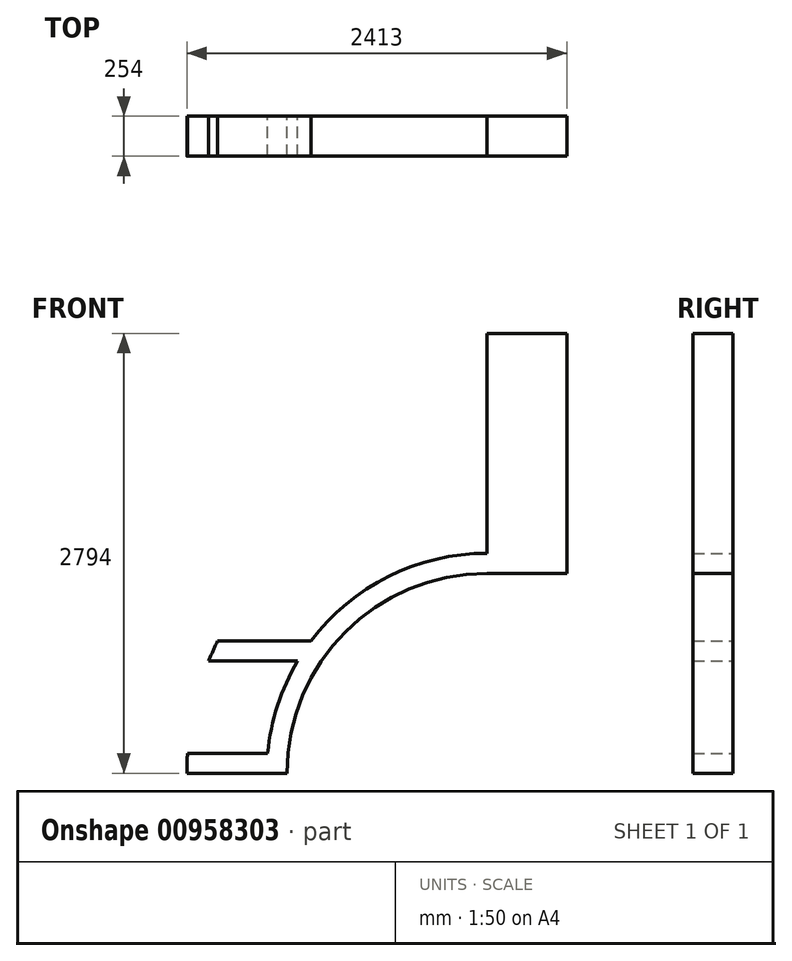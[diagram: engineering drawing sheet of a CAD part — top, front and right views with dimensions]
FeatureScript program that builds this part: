
annotation { "Feature Type Name" : "Feature", "Feature Type Description" : "" }
export const myFeature = defineFeature(function(context is Context, id is Id, definition is map)
    precondition{}
    {
        {
            var Q0;
            Q0=qCreatedBy(makeId("Front.planeOp"),FACE);
            var sketch = newSketch(context, id + "F0", { "sketchPlane" : qUnion([Q0])});
            skLineSegment(sketch, "E0", {"start": v(0, 0) * mm, "end": v(-2540, 0) * mm, "construction": true});
            skLineSegment(sketch, "E1", {"start": v(0, 0) * mm, "end": v(0, -2794) * mm, "construction": true});
            skLineSegment(sketch, "E2", {"start": v(-101.6, 0) * mm, "end": v(-101.6, -2655.82) * mm, "construction": true});
            skLineSegment(sketch, "E3", {"start": v(-304.8, 0) * mm, "end": v(-304.8, -2693.14) * mm, "construction": true});
            skLineSegment(sketch, "E4", {"start": v(-1748.8, 0) * mm, "end": v(-1748.79, -2667) * mm, "construction": true});
            skLineSegment(sketch, "E5", {"start": v(-762, 0) * mm, "end": v(-762, -2506.54) * mm, "construction": true});
            skLineSegment(sketch, "E6", {"start": v(-874.78, 0) * mm, "end": v(-874.78, -2403.9) * mm, "construction": true});
            skLineSegment(sketch, "E7", {"start": v(-508, 0) * mm, "end": v(-508, -2794) * mm});
            skLineSegment(sketch, "E8", {"start": v(-2540, 0) * mm, "end": v(-2540, -2684.02) * mm});
            skArc(sketch, "E9", {"start": v(-508, -1524) * mm, "mid": v(-1406.03, -1895.97) * mm, "end": v(-1778, -2794) * mm});
            skArc(sketch, "E10", {"start": v(-2540, -2794) * mm, "mid": v(-1944.84, -1357.16) * mm, "end": v(-508, -762) * mm});
            skArc(sketch, "E11", {"start": v(-2413, -2794) * mm, "mid": v(-1855.04, -1446.96) * mm, "end": v(-508, -889) * mm});
            skArc(sketch, "E12", {"start": v(-1905, -2794) * mm, "mid": v(-1495.83, -1806.17) * mm, "end": v(-508, -1397) * mm});
            skLineSegment(sketch, "E13", {"start": v(-2413, -2794) * mm, "end": v(-1905, -2794) * mm});
            skLineSegment(sketch, "E14", {"start": v(-1899.22, -2667) * mm, "end": v(-2408.76, -2667) * mm});
            skPoint(sketch, "E15.endSnap0", {"position": v(-1944.84, -1357.16) * mm});
            skLineSegment(sketch, "E16", {"start": v(-3837.1, -1954.53) * mm, "end": v(-1294.15, -1954.53) * mm, "construction": true});
            skLineSegment(sketch, "E17", {"start": v(-2218.06, -1954.53) * mm, "end": v(-1624.65, -1954.53) * mm});
            skLineSegment(sketch, "E18", {"start": v(-2274.75, -2081.53) * mm, "end": v(-1709.66, -2081.53) * mm});
            skLineSegment(sketch, "E19", {"start": v(-1624.65, -1954.53) * mm, "end": v(-1299.5, -1061.22) * mm});
            skLineSegment(sketch, "E20", {"start": v(-1466.04, -1147.43) * mm, "end": v(-1759.8, -1954.53) * mm});
            skLineSegment(sketch, "E21.bottom", {"start": v(-508, -1524) * mm, "end": v(0, -1524) * mm});
            skLineSegment(sketch, "E21.top", {"start": v(-508, 0) * mm, "end": v(0, 0) * mm});
            skLineSegment(sketch, "E21.left", {"start": v(-508, -1524) * mm, "end": v(-508, 0) * mm});
            skLineSegment(sketch, "E21.right", {"start": v(0, -1524) * mm, "end": v(0, 0) * mm});
            skLineSegment(sketch, "E22", {"start": v(-2540, -2794) * mm, "end": v(-1778, -2794) * mm});
            skSolve(sketch);
        }
        {
            var Q0;
            {var subQ0=sQuery(id+"F0.wireOp",EDGE,"E19");Q0=makeQuery(id+"F0.imprint","IMPRINT",FACE,{"disambiguationData":[TD([[makeQuery(id+"F0.imprint","IMPRINT",EDGE,{"derivedFrom":subQ0}),1.0]])]});}
            var sketch = newSketch(context, id + "F1", { "sketchPlane" : qUnion([Q0])});
            skSolve(sketch);
        }
        {
            var Q0;
            {var subQ3=sQuery(id+"F0.wireOp",EDGE,"E21.bottom");Q0=makeQuery(id+"F0.imprint","IMPRINT",FACE,{"disambiguationData":[TD([[makeQuery(id+"F0.imprint","IMPRINT",EDGE,{"derivedFrom":subQ3}),1.0]])]});}
            var Q1;
            {var subQ5=sQuery(id+"F0.wireOp",EDGE,"E10");Q1=makeQuery(id+"F0.imprint","IMPRINT",FACE,{"disambiguationData":[TD([[makeQuery(id+"F0.imprint","IMPRINT",EDGE,{"derivedFrom":subQ5}),-1.0]])]});}
            var Q2;
            {var subQ4=sQuery(id+"F0.wireOp",EDGE,"E9");Q2=makeQuery(id+"F0.imprint","IMPRINT",FACE,{"disambiguationData":[TD([[makeQuery(id+"F0.imprint","IMPRINT",EDGE,{"derivedFrom":subQ4}),-1.0]])]});}
            var Q3;
            {var subQ0=sQuery(id+"F0.wireOp",EDGE,"E19");Q3=makeQuery(id+"F1.imprint","IMPRINT",FACE,{"disambiguationData":[TD([[makeQuery(id+"F1.imprint","IMPRINT",EDGE,{"derivedFrom":makeQuery(id+"F0.imprint","IMPRINT",EDGE,{"derivedFrom":subQ0})}),1.0]])]});}
            var Q4;
            {var subQ6=sQuery(id+"F0.wireOp",EDGE,"E18");Q4=makeQuery(id+"F0.imprint","IMPRINT",FACE,{"disambiguationData":[TD([[makeQuery(id+"F0.imprint","IMPRINT",EDGE,{"derivedFrom":subQ6}),1.0]])]});}
            var Q5;
            {var subQ3=sQuery(id+"F0.wireOp",EDGE,"E14");Q5=makeQuery(id+"F0.imprint","IMPRINT",FACE,{"disambiguationData":[TD([[makeQuery(id+"F0.imprint","IMPRINT",EDGE,{"derivedFrom":subQ3}),1.0]])]});}
            extrude(context, id + "F2", {"entities" : qUnion([Q0, Q1, Q2, Q3, Q4, Q5]), "depth" : 254 * mm, "offsetDistance" : 25.4 * mm});
        }
    });
